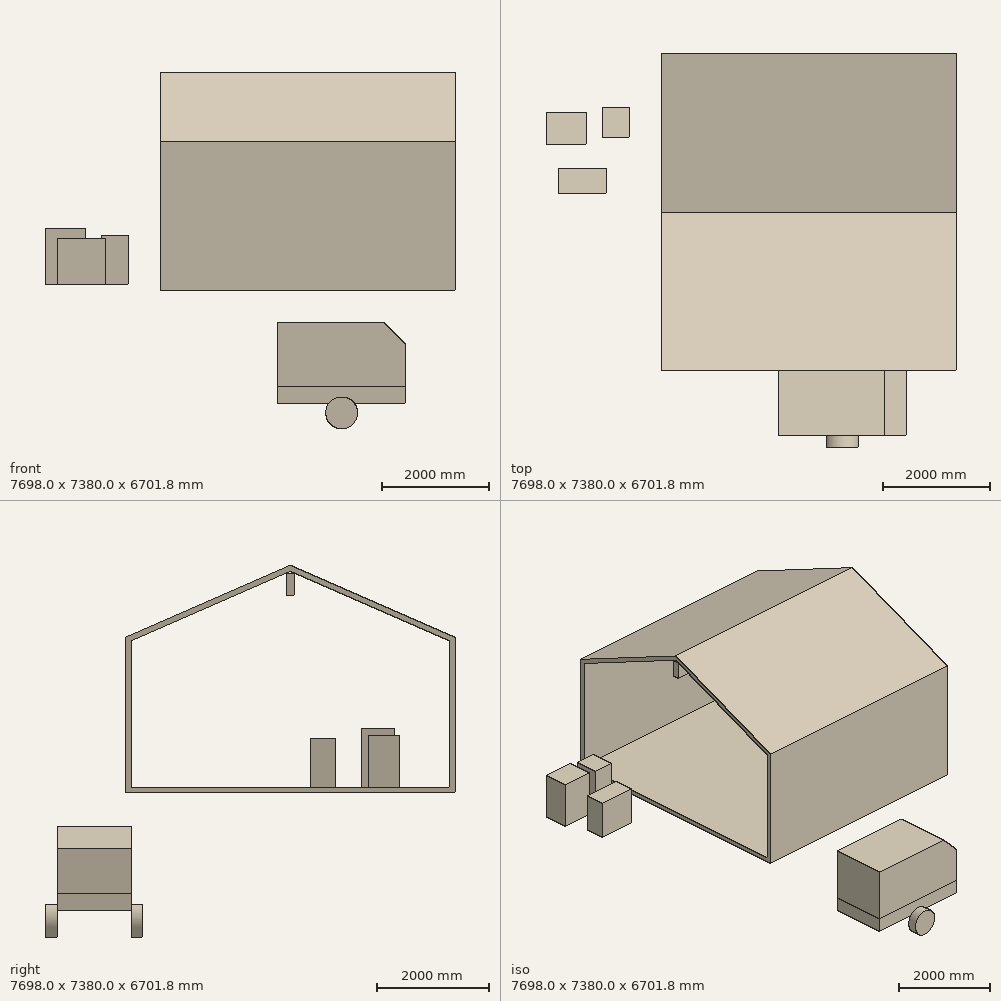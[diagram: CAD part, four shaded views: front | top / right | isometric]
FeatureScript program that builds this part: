
annotation { "Feature Type Name" : "Feature", "Feature Type Description" : "" }
export const myFeature = defineFeature(function(context is Context, id is Id, definition is map)
    precondition{}
    {
        {
            var Q0;
            Q0=qCreatedBy(makeId("Right.planeOp"),FACE);
            var sketch = newSketch(context, id + "F0", { "sketchPlane" : qUnion([Q0])});
            skLineSegment(sketch, "E0", {"start": v(0, 0) * mm, "end": v(5740, 0) * mm});
            skLineSegment(sketch, "E1", {"start": v(5740, 0) * mm, "end": v(5740, 2630) * mm});
            skLineSegment(sketch, "E2", {"start": v(5740, 2630) * mm, "end": v(2870, 3884.98) * mm});
            skLineSegment(sketch, "E3", {"start": v(2870, 3884.98) * mm, "end": v(0, 2630) * mm});
            skLineSegment(sketch, "E4", {"start": v(0, 2630) * mm, "end": v(0, 0) * mm});
            skLineSegment(sketch, "E5.bottom", {"start": v(2790, 3850) * mm, "end": v(2950, 3850) * mm});
            skLineSegment(sketch, "E5.top", {"start": v(2790, 3450) * mm, "end": v(2950, 3450) * mm});
            skLineSegment(sketch, "E5.left", {"start": v(2790, 3850) * mm, "end": v(2790, 3450) * mm});
            skLineSegment(sketch, "E5.right", {"start": v(2950, 3850) * mm, "end": v(2950, 3450) * mm});
            skLineSegment(sketch, "E6", {"start": v(2870, 3450) * mm, "end": v(2870, 0) * mm, "construction": true});
            skPoint(sketch, "E6.endSnap0", {"position": v(2870, 0) * mm});
            skLineSegment(sketch, "E7.0", {"start": v(-100, 2695.41) * mm, "end": v(-100, -100) * mm});
            skLineSegment(sketch, "E7.1", {"start": v(2870, 3994.12) * mm, "end": v(-100, 2695.41) * mm});
            skLineSegment(sketch, "E7.2", {"start": v(-100, -100) * mm, "end": v(5840, -100) * mm});
            skLineSegment(sketch, "E7.3", {"start": v(5840, -100) * mm, "end": v(5840, 2695.41) * mm});
            skLineSegment(sketch, "E7.4", {"start": v(5840, 2695.41) * mm, "end": v(2870, 3994.12) * mm});
            skSolve(sketch);
        }
        {
            var Q0;
            Q0=makeQuery(id+"F0.imprint","IMPRINT",FACE,{"disambiguationData":[TD([[makeQuery(id+"F0.imprint","IMPRINT",EDGE,{"derivedFrom":sQuery(id+"F0.wireOp",EDGE,"E0")}),-1.0]])]});
            var Q1;
            Q1=makeQuery(id+"F0.imprint","IMPRINT",FACE,{"disambiguationData":[TD([[makeQuery(id+"F0.imprint","IMPRINT",EDGE,{"derivedFrom":sQuery(id+"F0.wireOp",EDGE,"E5.bottom")}),-1.0]])]});
            extrude(context, id + "F1", {"entities" : qUnion([Q0, Q1]), "endBound" : BoundingType.SYMMETRIC, "depth" : 5530 * mm, "offsetDistance" : 25 * mm});
        }
        {
            var Q0;
            Q0=qCreatedBy(makeId("Front.planeOp"),FACE);
            var sketch = newSketch(context, id + "F2", { "sketchPlane" : qUnion([Q0])});
            skLineSegment(sketch, "E8.bottom", {"start": v(-577.96, -2227.68) * mm, "end": v(1822.04, -2227.68) * mm});
            skLineSegment(sketch, "E8.top", {"start": v(-577.96, -1907.68) * mm, "end": v(1822.04, -1907.68) * mm});
            skLineSegment(sketch, "E8.left", {"start": v(-577.96, -2227.68) * mm, "end": v(-577.96, -1907.68) * mm});
            skLineSegment(sketch, "E8.right", {"start": v(1822.04, -2227.68) * mm, "end": v(1822.04, -1907.68) * mm});
            skSolve(sketch);
        }
        {
            var Q0;
            Q0 = qSketchRegion(id + "F2", true);
            extrude(context, id + "F3", {"entities" : qUnion([Q0]), "depth" : (1290 + 2 * 20) * mm, "offsetDistance" : 25 * mm});
        }
        {
            var Q0;
            Q0=makeQuery(id+"F3.opExtrude","SWEPT_FACE",FACE,{"disambiguationData":[OSD([sQuery(id+"F2.wireOp",EDGE,"E8.top")])]});
            shell(context, id + "F4", {"entities" : qUnion([Q0]), "thickness" : 20 * mm});
        }
        {
            var Q0;
            Q0=makeQuery(id+"F3.opExtrude","CAP_FACE",FACE,{"disambiguationData":[OSD([sQuery(id+"F2.wireOp",EDGE,"E8.bottom"),sQuery(id+"F2.wireOp",EDGE,"E8.top"),sQuery(id+"F2.wireOp",EDGE,"E8.left"),sQuery(id+"F2.wireOp",EDGE,"E8.right")])],"isStart":false});
            var sketch = newSketch(context, id + "F5", { "sketchPlane" : qUnion([Q0])});
            skCircle(sketch, "E9", {"center": v(629.18, -2407.68) * mm, "radius": 300 * mm});
            skSolve(sketch);
        }
        {
            var Q0;
            Q0 = qSketchRegion(id + "F5", true);
            extrude(context, id + "F6", {"entities" : qUnion([Q0]), "operationType" : NewBodyOperationType.ADD, "depth" : 210 * mm, "offsetDistance" : 25 * mm});
        }
        {
            var Q0;
            Q0=makeQuery(id+"F3.opExtrude","CAP_FACE",FACE,{"disambiguationData":[OSD([sQuery(id+"F2.wireOp",EDGE,"E8.bottom"),sQuery(id+"F2.wireOp",EDGE,"E8.top"),sQuery(id+"F2.wireOp",EDGE,"E8.left"),sQuery(id+"F2.wireOp",EDGE,"E8.right")])],"isStart":true});
            var sketch = newSketch(context, id + "F7", { "sketchPlane" : qUnion([Q0])});
            skCircle(sketch, "E10.0", {"center": v(-629.18, -2407.68) * mm, "radius": 300 * mm});
            skSolve(sketch);
        }
        {
            var Q0;
            Q0 = qSketchRegion(id + "F7", true);
            extrude(context, id + "F8", {"entities" : qUnion([Q0]), "operationType" : NewBodyOperationType.ADD, "depth" : 210 * mm, "offsetDistance" : 25 * mm});
        }
        {
            var Q0;
            Q0=makeQuery(id+"F3.opExtrude","SWEPT_FACE",FACE,{"disambiguationData":[OSD([sQuery(id+"F2.wireOp",EDGE,"E8.top")])]});
            var sketch = newSketch(context, id + "F9", { "sketchPlane" : qUnion([Q0])});
            skLineSegment(sketch, "E11.bottom", {"start": v(-577.96, -1330) * mm, "end": v(1822.04, -1330) * mm});
            skLineSegment(sketch, "E11.top", {"start": v(-577.96, 0) * mm, "end": v(1822.04, 0) * mm});
            skLineSegment(sketch, "E11.left", {"start": v(-577.96, -1330) * mm, "end": v(-577.96, 0) * mm});
            skLineSegment(sketch, "E11.right", {"start": v(1822.04, -1330) * mm, "end": v(1822.04, 0) * mm});
            skSolve(sketch);
        }
        {
            var Q0;
            Q0 = qSketchRegion(id + "F9", true);
            extrude(context, id + "F10", {"entities" : qUnion([Q0]), "depth" : 1200 * mm, "offsetDistance" : 25 * mm});
        }
        {
            var Q0;
            Q0=makeQuery(id+"F10.opExtrude","CAP_EDGE",EDGE,{"disambiguationData":[OSD([sQuery(id+"F9.wireOp",EDGE,"E11.right")])],"isStart":false});
            chamfer(context, id + "F11", {"entities" : qUnion([Q0]), "width" : 400 * mm, "tangentPropagation" : true});
        }
        {
            var Q0;
            Q0=makeQuery(id+"F1.opExtrude","SWEPT_FACE",FACE,{"disambiguationData":[OSD([sQuery(id+"F0.wireOp",EDGE,"E0")])]});
            var sketch = newSketch(context, id + "F12", { "sketchPlane" : qUnion([Q0])});
            skLineSegment(sketch, "E12.bottom", {"start": v(-4933, 4747.92) * mm, "end": v(-4183, 4747.92) * mm});
            skLineSegment(sketch, "E12.top", {"start": v(-4933, 4147.92) * mm, "end": v(-4183, 4147.92) * mm});
            skLineSegment(sketch, "E12.left", {"start": v(-4933, 4747.92) * mm, "end": v(-4933, 4147.92) * mm});
            skLineSegment(sketch, "E12.right", {"start": v(-4183, 4747.92) * mm, "end": v(-4183, 4147.92) * mm});
            skLineSegment(sketch, "E13.bottom", {"start": v(-3880.66, 4828.05) * mm, "end": v(-3380.66, 4828.05) * mm});
            skLineSegment(sketch, "E13.top", {"start": v(-3880.66, 4268.05) * mm, "end": v(-3380.66, 4268.05) * mm});
            skLineSegment(sketch, "E13.left", {"start": v(-3880.66, 4828.05) * mm, "end": v(-3880.66, 4268.05) * mm});
            skLineSegment(sketch, "E13.right", {"start": v(-3380.66, 4828.05) * mm, "end": v(-3380.66, 4268.05) * mm});
            skLineSegment(sketch, "E14.bottom", {"start": v(-4703.19, 3687.28) * mm, "end": v(-3803.19, 3687.28) * mm});
            skLineSegment(sketch, "E14.top", {"start": v(-4703.19, 3227.28) * mm, "end": v(-3803.19, 3227.28) * mm});
            skLineSegment(sketch, "E14.left", {"start": v(-4703.19, 3687.28) * mm, "end": v(-4703.19, 3227.28) * mm});
            skLineSegment(sketch, "E14.right", {"start": v(-3803.19, 3687.28) * mm, "end": v(-3803.19, 3227.28) * mm});
            skSolve(sketch);
        }
        {
            var Q0;
            Q0=makeQuery(id+"F12.imprint","IMPRINT",FACE,{"disambiguationData":[TD([[makeQuery(id+"F12.imprint","IMPRINT",EDGE,{"derivedFrom":sQuery(id+"F12.wireOp",EDGE,"E12.bottom")}),-1.0]])]});
            extrude(context, id + "F13", {"entities" : qUnion([Q0]), "depth" : 1060 * mm, "offsetDistance" : 25 * mm});
        }
        {
            var Q0;
            Q0=makeQuery(id+"F12.imprint","IMPRINT",FACE,{"disambiguationData":[TD([[makeQuery(id+"F12.imprint","IMPRINT",EDGE,{"derivedFrom":sQuery(id+"F12.wireOp",EDGE,"E13.bottom")}),-1.0]])]});
            extrude(context, id + "F14", {"entities" : qUnion([Q0]), "depth" : 930 * mm, "offsetDistance" : 25 * mm});
        }
        {
            var Q0;
            Q0=makeQuery(id+"F12.imprint","IMPRINT",FACE,{"disambiguationData":[TD([[makeQuery(id+"F12.imprint","IMPRINT",EDGE,{"derivedFrom":sQuery(id+"F12.wireOp",EDGE,"E14.bottom")}),-1.0]])]});
            extrude(context, id + "F15", {"entities" : qUnion([Q0]), "depth" : 870 * mm, "offsetDistance" : 25 * mm});
        }
    });
